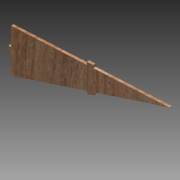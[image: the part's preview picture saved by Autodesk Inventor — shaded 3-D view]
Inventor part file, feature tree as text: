
AUTODESK INVENTOR PART (.ipt)
format: ipt  version: 2015 (Build 190159000, 159)  size: 126,976 bytes
history: native  units: in
note: dims shown in document units (in); Inventor stores cm internally (conversion verified against a paired STEP export)
features: sketch x3, extrude x2
ambient origin geometry x8: Origin, YZ Plane, XZ Plane, XY Plane, X Axis, Y Axis, Z Axis, Center Point
bodies: Solid1 (feature_tree)
feature tree (5):
  extrude  "Extrusion1"  Depth=0.125in TaperAngle=0.0deg
  extrude  "Extrusion5"  Depth=0.3in
  sketch  "Sketch6"  dims[d37=0.15in d38=0.125in d39=0.15in d40=0.3in d41=0.125in d42=0.15in d44=0.3in d45=0.125in d46=0.125in d47=0.0in d48=0.639in]
  sketch  "Sketch1"  dims[d0=2.084in d2=0.125in d3=0.0in]
  sketch  "Sketch5"  dims[d34=0.1036in d36=0.3in]
